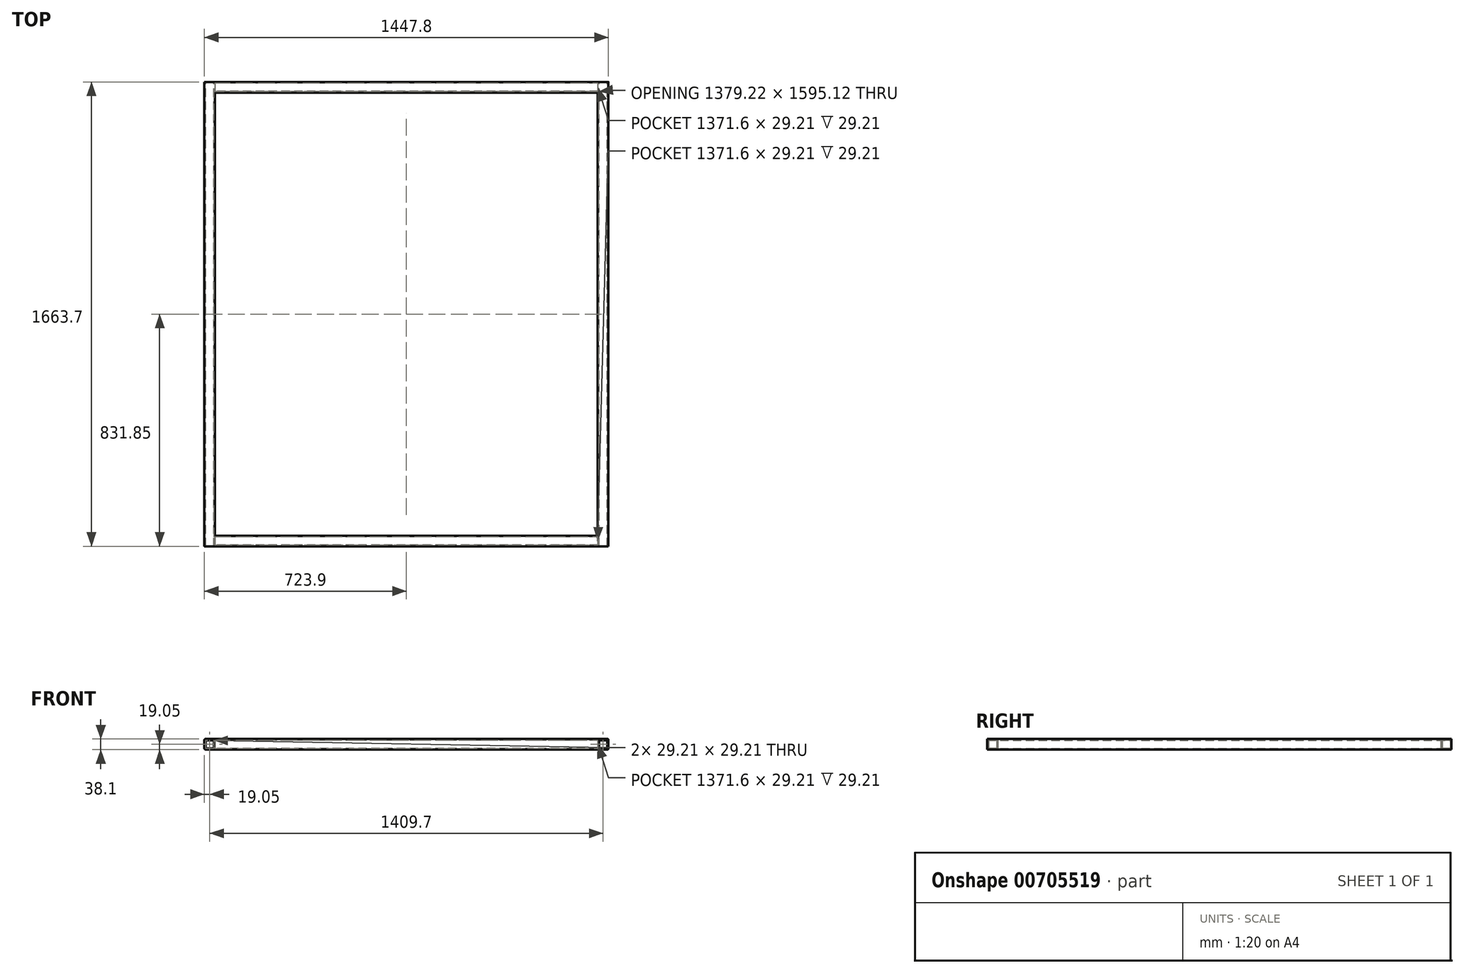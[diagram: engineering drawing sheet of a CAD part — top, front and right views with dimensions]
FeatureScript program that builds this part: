
annotation { "Feature Type Name" : "Feature", "Feature Type Description" : "" }
export const myFeature = defineFeature(function(context is Context, id is Id, definition is map)
    precondition{}
    {
        {
            var Q0;
            Q0=qCreatedBy(makeId("Top.planeOp"),FACE);
            var sketch = newSketch(context, id + "F0", { "sketchPlane" : qUnion([Q0])});
            skLineSegment(sketch, "E0", {"start": v(0, 0) * mm, "end": v(704.85, 0) * mm, "construction": true});
            skLineSegment(sketch, "E1", {"start": v(0, 0) * mm, "end": v(-704.85, 0) * mm, "construction": true});
            skLineSegment(sketch, "E2", {"start": v(0, 0) * mm, "end": v(0, 812.8) * mm, "construction": true});
            skLineSegment(sketch, "E3", {"start": v(0, 0) * mm, "end": v(0, -812.8) * mm, "construction": true});
            skSolve(sketch);
        }
        {
            var Q0;
            Q0=qCreatedBy(makeId("Front.planeOp"),FACE);
            var sketch = newSketch(context, id + "F1", { "sketchPlane" : qUnion([Q0])});
            skLineSegment(sketch, "E4.bottom", {"start": v(-689.6, 19.05) * mm, "end": v(-720.1, 19.05) * mm});
            skLineSegment(sketch, "E4.top", {"start": v(-689.6, -19.05) * mm, "end": v(-720.1, -19.05) * mm});
            skLineSegment(sketch, "E4.left", {"start": v(-685.8, 15.24) * mm, "end": v(-685.8, -15.24) * mm});
            skLineSegment(sketch, "E4.right", {"start": v(-723.9, 15.24) * mm, "end": v(-723.9, -15.24) * mm});
            skPoint(sketch, "E4.middle", {"position": v(-704.85, 0) * mm});
            skLineSegment(sketch, "E5.bottom", {"start": v(720.1, 19.05) * mm, "end": v(689.6, 19.05) * mm});
            skLineSegment(sketch, "E5.top", {"start": v(720.1, -19.05) * mm, "end": v(689.6, -19.05) * mm});
            skLineSegment(sketch, "E5.left", {"start": v(723.9, 15.24) * mm, "end": v(723.9, -15.24) * mm});
            skLineSegment(sketch, "E5.right", {"start": v(685.8, 15.24) * mm, "end": v(685.8, -15.24) * mm});
            skPoint(sketch, "E5.middle", {"position": v(704.85, 0) * mm});
            skPoint(sketch, "E6.visualSharp", {"position": v(-723.9, 19.05) * mm});
            skArc(sketch, "E6.filletArc", {"start": v(-720.1, 19.05) * mm, "mid": v(-722.78, 17.93) * mm, "end": v(-723.9, 15.24) * mm});
            skPoint(sketch, "E7.visualSharp", {"position": v(-685.8, 19.05) * mm});
            skArc(sketch, "E7.filletArc", {"start": v(-685.8, 15.24) * mm, "mid": v(-686.92, 17.93) * mm, "end": v(-689.6, 19.05) * mm});
            skPoint(sketch, "E8.visualSharp", {"position": v(-685.8, -19.05) * mm});
            skArc(sketch, "E8.filletArc", {"start": v(-689.6, -19.05) * mm, "mid": v(-686.92, -17.93) * mm, "end": v(-685.8, -15.24) * mm});
            skPoint(sketch, "E9.visualSharp", {"position": v(-723.9, -19.05) * mm});
            skArc(sketch, "E9.filletArc", {"start": v(-723.9, -15.24) * mm, "mid": v(-722.78, -17.93) * mm, "end": v(-720.1, -19.05) * mm});
            skPoint(sketch, "E10.visualSharp", {"position": v(685.8, 19.05) * mm});
            skArc(sketch, "E10.filletArc", {"start": v(689.6, 19.05) * mm, "mid": v(686.92, 17.93) * mm, "end": v(685.8, 15.24) * mm});
            skPoint(sketch, "E11.visualSharp", {"position": v(723.9, 19.05) * mm});
            skArc(sketch, "E11.filletArc", {"start": v(723.9, 15.24) * mm, "mid": v(722.78, 17.93) * mm, "end": v(720.1, 19.05) * mm});
            skPoint(sketch, "E12.visualSharp", {"position": v(723.9, -19.05) * mm});
            skArc(sketch, "E12.filletArc", {"start": v(720.1, -19.05) * mm, "mid": v(722.78, -17.93) * mm, "end": v(723.9, -15.24) * mm});
            skPoint(sketch, "E13.visualSharp", {"position": v(685.8, -19.05) * mm});
            skArc(sketch, "E13.filletArc", {"start": v(685.8, -15.24) * mm, "mid": v(686.92, -17.93) * mm, "end": v(689.6, -19.05) * mm});
            skLineSegment(sketch, "E14.0", {"start": v(-690.25, 14.6) * mm, "end": v(-719.46, 14.6) * mm});
            skLineSegment(sketch, "E14.1", {"start": v(-690.25, 14.6) * mm, "end": v(-690.25, -14.6) * mm});
            skLineSegment(sketch, "E14.2", {"start": v(-690.25, -14.6) * mm, "end": v(-719.46, -14.6) * mm});
            skLineSegment(sketch, "E14.3", {"start": v(-719.46, 14.6) * mm, "end": v(-719.46, -14.6) * mm});
            skLineSegment(sketch, "E15.0", {"start": v(719.46, 14.6) * mm, "end": v(690.25, 14.6) * mm});
            skLineSegment(sketch, "E15.1", {"start": v(719.46, 14.6) * mm, "end": v(719.46, -14.6) * mm});
            skLineSegment(sketch, "E15.2", {"start": v(719.46, -14.6) * mm, "end": v(690.25, -14.6) * mm});
            skLineSegment(sketch, "E15.3", {"start": v(690.25, 14.6) * mm, "end": v(690.25, -14.6) * mm});
            skSolve(sketch);
        }
        {
            var Q0;
            Q0 = qSketchRegion(id + "F1", true);
            extrude(context, id + "F2", {"entities" : qUnion([Q0]), "endBound" : BoundingType.SYMMETRIC, "depth" : 1663.7 * mm, "offsetDistance" : 25.4 * mm});
        }
        {
            var Q0;
            Q0=qCreatedBy(makeId("Right.planeOp"),FACE);
            var sketch = newSketch(context, id + "F3", { "sketchPlane" : qUnion([Q0])});
            skLineSegment(sketch, "E16.bottom", {"start": v(-797.56, 19.05) * mm, "end": v(-828.04, 19.05) * mm});
            skLineSegment(sketch, "E16.top", {"start": v(-797.56, -19.05) * mm, "end": v(-828.04, -19.05) * mm});
            skLineSegment(sketch, "E16.left", {"start": v(-793.75, 15.24) * mm, "end": v(-793.75, -15.24) * mm});
            skLineSegment(sketch, "E16.right", {"start": v(-831.85, 15.24) * mm, "end": v(-831.85, -15.24) * mm});
            skPoint(sketch, "E16.middle", {"position": v(-812.8, 0) * mm});
            skLineSegment(sketch, "E17.bottom", {"start": v(828.04, 19.05) * mm, "end": v(797.56, 19.05) * mm});
            skLineSegment(sketch, "E17.top", {"start": v(828.04, -19.05) * mm, "end": v(797.56, -19.05) * mm});
            skLineSegment(sketch, "E17.left", {"start": v(831.85, 15.24) * mm, "end": v(831.85, -15.24) * mm});
            skLineSegment(sketch, "E17.right", {"start": v(793.75, 15.24) * mm, "end": v(793.75, -15.24) * mm});
            skPoint(sketch, "E17.middle", {"position": v(812.8, 0) * mm});
            skPoint(sketch, "E18.visualSharp", {"position": v(-831.85, 19.05) * mm});
            skArc(sketch, "E18.filletArc", {"start": v(-828.04, 19.05) * mm, "mid": v(-830.73, 17.93) * mm, "end": v(-831.85, 15.24) * mm});
            skPoint(sketch, "E19.visualSharp", {"position": v(-793.75, -19.05) * mm});
            skArc(sketch, "E19.filletArc", {"start": v(-797.56, -19.05) * mm, "mid": v(-794.87, -17.93) * mm, "end": v(-793.75, -15.24) * mm});
            skPoint(sketch, "E20.visualSharp", {"position": v(-831.85, -19.05) * mm});
            skArc(sketch, "E20.filletArc", {"start": v(-831.85, -15.24) * mm, "mid": v(-830.73, -17.93) * mm, "end": v(-828.04, -19.05) * mm});
            skPoint(sketch, "E21.visualSharp", {"position": v(-793.75, 19.05) * mm});
            skArc(sketch, "E21.filletArc", {"start": v(-793.75, 15.24) * mm, "mid": v(-794.87, 17.93) * mm, "end": v(-797.56, 19.05) * mm});
            skPoint(sketch, "E22.visualSharp", {"position": v(793.75, -19.05) * mm});
            skArc(sketch, "E22.filletArc", {"start": v(793.75, -15.24) * mm, "mid": v(794.87, -17.93) * mm, "end": v(797.56, -19.05) * mm});
            skPoint(sketch, "E23.visualSharp", {"position": v(793.75, 19.05) * mm});
            skArc(sketch, "E23.filletArc", {"start": v(797.56, 19.05) * mm, "mid": v(794.87, 17.93) * mm, "end": v(793.75, 15.24) * mm});
            skPoint(sketch, "E24.visualSharp", {"position": v(831.85, 19.05) * mm});
            skArc(sketch, "E24.filletArc", {"start": v(831.85, 15.24) * mm, "mid": v(830.73, 17.93) * mm, "end": v(828.04, 19.05) * mm});
            skPoint(sketch, "E25.visualSharp", {"position": v(831.85, -19.05) * mm});
            skArc(sketch, "E25.filletArc", {"start": v(828.04, -19.05) * mm, "mid": v(830.73, -17.93) * mm, "end": v(831.85, -15.24) * mm});
            skLineSegment(sketch, "E26.0", {"start": v(827.4, 14.6) * mm, "end": v(798.2, 14.6) * mm});
            skLineSegment(sketch, "E26.1", {"start": v(827.4, 14.6) * mm, "end": v(827.4, -14.6) * mm});
            skLineSegment(sketch, "E26.2", {"start": v(827.4, -14.6) * mm, "end": v(798.2, -14.6) * mm});
            skLineSegment(sketch, "E26.3", {"start": v(798.2, 14.6) * mm, "end": v(798.2, -14.6) * mm});
            skLineSegment(sketch, "E27.0", {"start": v(-798.2, 14.6) * mm, "end": v(-827.4, 14.6) * mm});
            skLineSegment(sketch, "E27.1", {"start": v(-798.2, 14.6) * mm, "end": v(-798.2, -14.6) * mm});
            skLineSegment(sketch, "E27.2", {"start": v(-798.2, -14.6) * mm, "end": v(-827.4, -14.6) * mm});
            skLineSegment(sketch, "E27.3", {"start": v(-827.4, 14.6) * mm, "end": v(-827.4, -14.6) * mm});
            skSolve(sketch);
        }
        {
            var Q0;
            Q0 = qSketchRegion(id + "F3", true);
            extrude(context, id + "F4", {"entities" : qUnion([Q0]), "operationType" : NewBodyOperationType.ADD, "endBound" : BoundingType.SYMMETRIC, "depth" : 1371.6 * mm, "offsetDistance" : 25.4 * mm});
        }
        {
            var Q0;
            Q0=makeQuery(id+"F4.boolean.opBoolean","MERGE",FACE,{"derivedFrom":[makeQuery(id+"F2.opExtrude","CAP_FACE",FACE,{"disambiguationData":[OSD([sQuery(id+"F1.wireOp",EDGE,"E4.bottom"),sQuery(id+"F1.wireOp",EDGE,"E4.top"),sQuery(id+"F1.wireOp",EDGE,"E4.left"),sQuery(id+"F1.wireOp",EDGE,"E4.right"),sQuery(id+"F1.wireOp",EDGE,"E6.filletArc"),sQuery(id+"F1.wireOp",EDGE,"E7.filletArc"),sQuery(id+"F1.wireOp",EDGE,"E8.filletArc"),sQuery(id+"F1.wireOp",EDGE,"E9.filletArc"),sQuery(id+"F1.wireOp",EDGE,"E14.0"),sQuery(id+"F1.wireOp",EDGE,"E14.1"),sQuery(id+"F1.wireOp",EDGE,"E14.2"),sQuery(id+"F1.wireOp",EDGE,"E14.3")])],"isStart":false}),makeQuery(id+"F2.opExtrude","CAP_FACE",FACE,{"disambiguationData":[OSD([sQuery(id+"F1.wireOp",EDGE,"E5.bottom"),sQuery(id+"F1.wireOp",EDGE,"E5.top"),sQuery(id+"F1.wireOp",EDGE,"E5.left"),sQuery(id+"F1.wireOp",EDGE,"E5.right"),sQuery(id+"F1.wireOp",EDGE,"E10.filletArc"),sQuery(id+"F1.wireOp",EDGE,"E11.filletArc"),sQuery(id+"F1.wireOp",EDGE,"E12.filletArc"),sQuery(id+"F1.wireOp",EDGE,"E13.filletArc"),sQuery(id+"F1.wireOp",EDGE,"E15.0"),sQuery(id+"F1.wireOp",EDGE,"E15.1"),sQuery(id+"F1.wireOp",EDGE,"E15.2"),sQuery(id+"F1.wireOp",EDGE,"E15.3")])],"isStart":false}),makeQuery(id+"F4.opExtrude","SWEPT_FACE",FACE,{"disambiguationData":[OSD([sQuery(id+"F3.wireOp",EDGE,"E16.right")])]})]});
            cPlane(context, id + "F5", {"entities" : qUnion([Q0]), "cplaneType" : CPlaneType.OFFSET, "offset" : 0 * mm, "width" : 152.4 * mm, "height" : 152.4 * mm});
        }
        {
            var Q0;
            Q0=qCreatedBy(id+"F5.planeOp",FACE);
            var sketch = newSketch(context, id + "F6", { "sketchPlane" : qUnion([Q0])});
            skLineSegment(sketch, "E28", {"start": v(-685.8, 19.05) * mm, "end": v(-685.8, 15.24) * mm});
            skLineSegment(sketch, "E29", {"start": v(-685.8, 19.05) * mm, "end": v(-689.6, 19.05) * mm});
            skLineSegment(sketch, "E30", {"start": v(-689.6, 19.05) * mm, "end": v(-685.8, 15.24) * mm});
            skLineSegment(sketch, "E31.MirrorCS", {"start": v(689.6, 19.05) * mm, "end": v(685.8, 15.24) * mm});
            skLineSegment(sketch, "E32.MirrorCS", {"start": v(685.8, 19.05) * mm, "end": v(689.6, 19.05) * mm});
            skLineSegment(sketch, "E33.MirrorCS", {"start": v(685.8, 19.05) * mm, "end": v(685.8, 15.24) * mm});
            skLineSegment(sketch, "E34.MirrorCS", {"start": v(-685.8, -19.05) * mm, "end": v(-685.8, -15.24) * mm});
            skLineSegment(sketch, "E35.MirrorCS", {"start": v(-685.8, -19.05) * mm, "end": v(-689.6, -19.05) * mm});
            skLineSegment(sketch, "E36.MirrorCS", {"start": v(-689.6, -19.05) * mm, "end": v(-685.8, -15.24) * mm});
            skLineSegment(sketch, "E37.MirrorCS", {"start": v(685.8, -19.05) * mm, "end": v(685.8, -15.24) * mm});
            skLineSegment(sketch, "E38.MirrorCS", {"start": v(685.8, -19.05) * mm, "end": v(689.6, -19.05) * mm});
            skLineSegment(sketch, "E39.MirrorCS", {"start": v(689.6, -19.05) * mm, "end": v(685.8, -15.24) * mm});
            skSolve(sketch);
        }
        {
            var Q0;
            Q0 = qSketchRegion(id + "F6", true);
            extrude(context, id + "F7", {"entities" : qUnion([Q0]), "operationType" : NewBodyOperationType.ADD, "oppositeDirection" : true, "depth" : 38.1 * mm, "offsetDistance" : 25.4 * mm});
        }
        {
            var Q0;
            Q0=makeQuery(id+"F4.boolean.opBoolean","MERGE",FACE,{"derivedFrom":[makeQuery(id+"F2.opExtrude","CAP_FACE",FACE,{"disambiguationData":[OSD([sQuery(id+"F1.wireOp",EDGE,"E4.bottom"),sQuery(id+"F1.wireOp",EDGE,"E4.top"),sQuery(id+"F1.wireOp",EDGE,"E4.left"),sQuery(id+"F1.wireOp",EDGE,"E4.right"),sQuery(id+"F1.wireOp",EDGE,"E6.filletArc"),sQuery(id+"F1.wireOp",EDGE,"E7.filletArc"),sQuery(id+"F1.wireOp",EDGE,"E8.filletArc"),sQuery(id+"F1.wireOp",EDGE,"E9.filletArc"),sQuery(id+"F1.wireOp",EDGE,"E14.0"),sQuery(id+"F1.wireOp",EDGE,"E14.1"),sQuery(id+"F1.wireOp",EDGE,"E14.2"),sQuery(id+"F1.wireOp",EDGE,"E14.3")])],"isStart":true}),makeQuery(id+"F2.opExtrude","CAP_FACE",FACE,{"disambiguationData":[OSD([sQuery(id+"F1.wireOp",EDGE,"E5.bottom"),sQuery(id+"F1.wireOp",EDGE,"E5.top"),sQuery(id+"F1.wireOp",EDGE,"E5.left"),sQuery(id+"F1.wireOp",EDGE,"E5.right"),sQuery(id+"F1.wireOp",EDGE,"E10.filletArc"),sQuery(id+"F1.wireOp",EDGE,"E11.filletArc"),sQuery(id+"F1.wireOp",EDGE,"E12.filletArc"),sQuery(id+"F1.wireOp",EDGE,"E13.filletArc"),sQuery(id+"F1.wireOp",EDGE,"E15.0"),sQuery(id+"F1.wireOp",EDGE,"E15.1"),sQuery(id+"F1.wireOp",EDGE,"E15.2"),sQuery(id+"F1.wireOp",EDGE,"E15.3")])],"isStart":true}),makeQuery(id+"F4.opExtrude","SWEPT_FACE",FACE,{"disambiguationData":[OSD([sQuery(id+"F3.wireOp",EDGE,"E17.left")])]})]});
            cPlane(context, id + "F8", {"entities" : qUnion([Q0]), "cplaneType" : CPlaneType.OFFSET, "offset" : 0 * mm, "width" : 152.4 * mm, "height" : 152.4 * mm});
        }
        {
            var Q0;
            Q0=qCreatedBy(id+"F8.planeOp",FACE);
            var sketch = newSketch(context, id + "F9", { "sketchPlane" : qUnion([Q0])});
            skLineSegment(sketch, "E40", {"start": v(-685.8, 19.05) * mm, "end": v(-685.8, 15.24) * mm});
            skLineSegment(sketch, "E41", {"start": v(-685.8, 19.05) * mm, "end": v(-689.6, 19.05) * mm});
            skLineSegment(sketch, "E42", {"start": v(-689.6, 19.05) * mm, "end": v(-685.8, 15.24) * mm});
            skLineSegment(sketch, "E43.MirrorCS", {"start": v(685.8, 19.05) * mm, "end": v(689.6, 19.05) * mm});
            skLineSegment(sketch, "E44.MirrorCS", {"start": v(685.8, 19.05) * mm, "end": v(685.8, 15.24) * mm});
            skLineSegment(sketch, "E45.MirrorCS", {"start": v(689.6, 19.05) * mm, "end": v(685.8, 15.24) * mm});
            skLineSegment(sketch, "E46.MirrorCS", {"start": v(685.8, -19.05) * mm, "end": v(689.6, -19.05) * mm});
            skLineSegment(sketch, "E47.MirrorCS", {"start": v(685.8, -19.05) * mm, "end": v(685.8, -15.24) * mm});
            skLineSegment(sketch, "E48.MirrorCS", {"start": v(689.61, -19.05) * mm, "end": v(685.8, -15.24) * mm});
            skLineSegment(sketch, "E49.MirrorCS", {"start": v(-685.8, -19.05) * mm, "end": v(-689.6, -19.05) * mm});
            skLineSegment(sketch, "E50.MirrorCS", {"start": v(-685.8, -19.05) * mm, "end": v(-685.8, -15.24) * mm});
            skLineSegment(sketch, "E51.MirrorCS", {"start": v(-689.6, -19.05) * mm, "end": v(-685.8, -15.24) * mm});
            skSolve(sketch);
        }
        {
            var Q0;
            Q0 = qSketchRegion(id + "F9", true);
            extrude(context, id + "F10", {"entities" : qUnion([Q0]), "operationType" : NewBodyOperationType.ADD, "oppositeDirection" : true, "depth" : 38.1 * mm, "offsetDistance" : 25.4 * mm});
        }
    });
